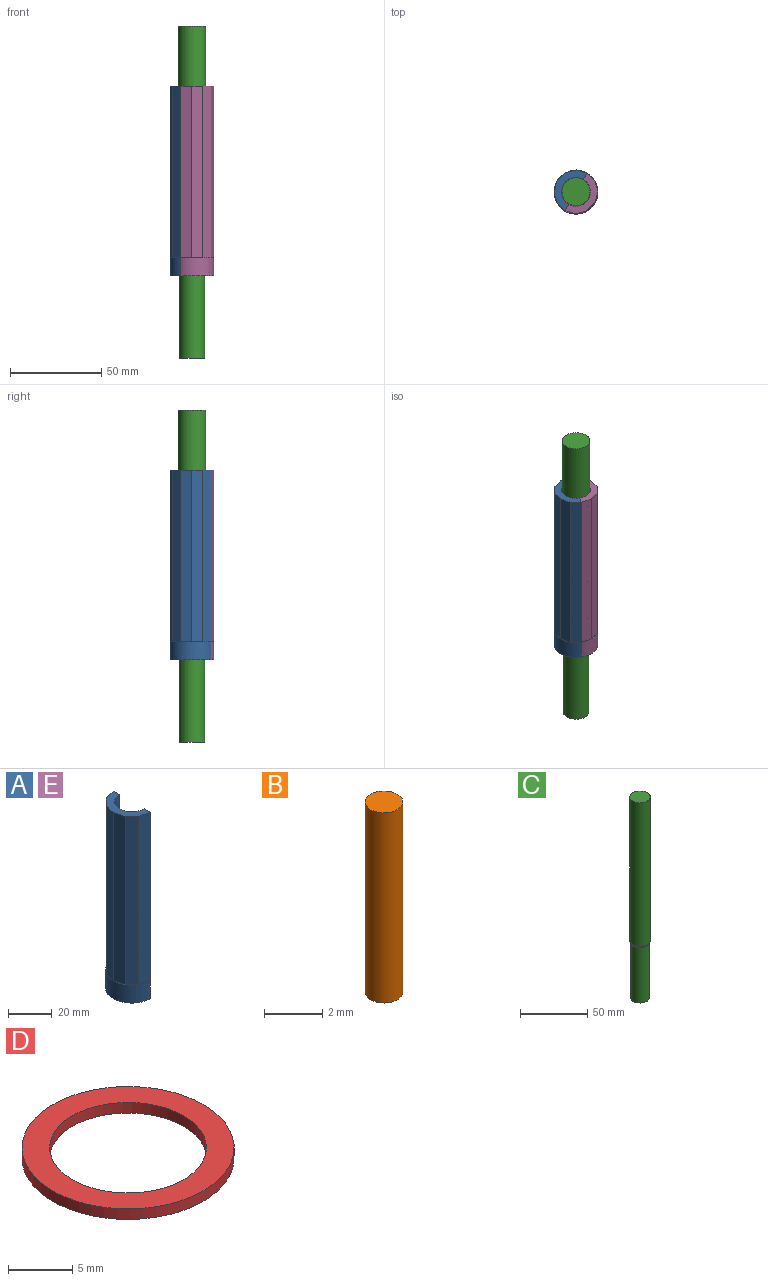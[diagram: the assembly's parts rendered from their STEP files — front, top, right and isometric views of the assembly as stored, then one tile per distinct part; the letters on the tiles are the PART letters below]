
ASSEMBLY  parts=5 mates=4
PART A: 38 faces, bbox 12x24x104 mm
  f0: plane 104x4.1mm, normal (1,0,0), area 417.7mm2, adj f11,f13,f14,f15,f16,f17,f18,f19
  f1: plane 94x4.39mm, normal (-0.71,-0.71,0), area 583.9mm2, adj f2,f9,f11,f12
  f2: plane 94x6mm, normal (-0.97,-0.26,0), area 583.9mm2, adj f1,f3,f8,f11
  f3: plane 94x6mm, normal (-0.97,0.26,0), area 583.9mm2, adj f2,f4,f7,f11
  f4: plane 94x4.39mm, normal (-0.71,0.71,0), area 583.9mm2, adj f3,f6,f11,f13
  f5: plane 6x1.61mm, normal (0,0,1), area 1.7mm2, adj f13,f19
  f6: plane 4.39x4.39mm, normal (0,0,1), area 1.7mm2, adj f4,f19
  f7: plane 6x1.61mm, normal (0,0,1), area 1.7mm2, adj f3,f19
  f8: plane 6x1.61mm, normal (0,0,1), area 1.7mm2, adj f2,f19
  f9: plane 4.39x4.39mm, normal (0,0,1), area 1.7mm2, adj f1,f19
  f10: plane 6x1.61mm, normal (0,0,1), area 1.7mm2, adj f12,f19
  f11: plane 24x12mm, normal (0,0,1), area 118mm2, adj f0,f1,f2,f3,f4,f12,f13,f20
  f12: plane 94x6mm, normal (-0.26,-0.97,0), area 583.9mm2, adj f1,f10,f11,f21
  f13: plane 94x6mm, normal (-0.26,0.97,0), area 583.9mm2, adj f0,f4,f5,f11
  f14: cylinder r=8.75mm len=17.5mm, axis (0,0,1), area 110mm2, adj f0,f15,f16,f21
  f15: plane 17.5x8.75mm, normal (0,0,-1), area 22.2mm2, adj f0,f14,f20,f21
  f16: plane 17.5x8.75mm, normal (0,0,1), area 22.2mm2, adj f0,f14,f17,f21
  f17: cylinder r=7.9mm len=15.8mm, axis (0,0,-1), area 74.5mm2, adj f0,f16,f18,f21
  f18: plane 24x12mm, normal (0,0,-1), area 128.2mm2, adj f0,f17,f19,f21
  f19: cylinder r=12mm len=24mm, axis (0,0,1), area 377mm2, adj f0,f5,f6,f7,f8,f9,f10,f18
  f20: cylinder r=7.9mm len=97mm, axis (0,0,-1), area 2407.4mm2, adj f0,f11,f15,f21
  f21: plane 104x4.1mm, normal (1,0,0), area 417.7mm2, adj f11,f12,f14,f15,f16,f17,f18,f19
  f22: cylinder r=0.65mm len=4mm, axis (1,0,0), area 16.3mm2, adj f21,f23
  f23: plane 1.3x1.3mm, normal (1,0,0), area 1.3mm2, adj f22
  f24: cylinder r=0.65mm len=4mm, axis (1,0,0), area 16.3mm2, adj f21,f25
  f25: plane 1.3x1.3mm, normal (1,0,0), area 1.3mm2, adj f24
  f26: cylinder r=0.65mm len=4mm, axis (1,0,0), area 16.3mm2, adj f21,f27
  f27: plane 1.3x1.3mm, normal (1,0,0), area 1.3mm2, adj f26
  f28: cylinder r=0.65mm len=4mm, axis (1,0,0), area 16.3mm2, adj f21,f29
  f29: plane 1.3x1.3mm, normal (1,0,0), area 1.3mm2, adj f28
  f30: cylinder r=0.65mm len=4mm, axis (1,0,0), area 16.3mm2, adj f0,f31
  f31: plane 1.3x1.3mm, normal (1,0,0), area 1.3mm2, adj f30
  f32: cylinder r=0.65mm len=4mm, axis (1,0,0), area 16.3mm2, adj f0,f33
  f33: plane 1.3x1.3mm, normal (1,0,0), area 1.3mm2, adj f32
  f34: cylinder r=0.65mm len=4mm, axis (1,0,0), area 16.3mm2, adj f0,f35
  f35: plane 1.3x1.3mm, normal (1,0,0), area 1.3mm2, adj f34
  f36: cylinder r=0.65mm len=4mm, axis (1,0,0), area 16.3mm2, adj f0,f37
  f37: plane 1.3x1.3mm, normal (1,0,0), area 1.3mm2, adj f36
PART B: 3 faces, bbox 1.3x1.3x8 mm
  f0: cylinder r=0.65mm len=8mm, axis (0,0,-1), area 32.7mm2, adj f1,f2
  f1: plane 1.3x1.3mm, normal (0,0,1), area 1.3mm2, adj f0
  f2: plane 1.3x1.3mm, normal (0,0,-1), area 1.3mm2, adj f0
PART C: 7 faces, bbox 15.3x15.3x182 mm
  f0: cylinder r=7mm len=50mm, axis (0,0,-1), area 2199.1mm2, adj f1,f2
  f1: plane 14x14mm, normal (0,0,1), area 40.8mm2, adj f0,f3
  f2: plane 14x14mm, normal (0,0,-1), area 153.9mm2, adj f0
  f3: cylinder r=6mm len=12mm, axis (0,0,-1), area 75.4mm2, adj f1,f6
  f4: cylinder r=7.65mm len=130mm, axis (0,0,-1), area 6248.6mm2, adj f5,f6
  f5: plane 15.3x15.3mm, normal (0,0,1), area 183.9mm2, adj f4
  f6: plane 15.3x15.3mm, normal (0,0,-1), area 70.8mm2, adj f3,f4
PART D: 4 faces, bbox 16.5x16.5x1 mm
  f0: cylinder r=6.1mm len=12.2mm, axis (0,0,-1), area 38.3mm2, adj f2,f3
  f1: cylinder r=8.25mm len=16.5mm, axis (0,0,-1), area 51.8mm2, adj f2,f3
  f2: plane 16.5x16.5mm, normal (0,0,1), area 96.9mm2, adj f0,f1
  f3: plane 16.5x16.5mm, normal (0,0,-1), area 96.9mm2, adj f0,f1
PART E: same geometry as A
PLACE A rot(axis=(0,0,-1),30.6deg) t=(1.16,1.81,90.67)mm
PLACE B rot(axis=(-0.78,-0.44,0.44),104.2deg) t=(-0.49,-8.84,105.23)mm
PLACE C rot(axis=(0,0,-1),30.6deg) t=(1.16,1.81,35.67)mm fixed
PLACE D rot(axis=(0,0,-1),30.6deg) t=(1.16,1.81,86.67)mm
PLACE E rot(axis=(0,0,1),149.4deg) t=(1.16,1.81,90.67)mm
MATE slider C.f4 <-> A.f17  axis (0,0,-1) through (1.16,1.81,87.67)mm
MATE fastened E.f30 <-> B.f0  axis (-0.86,0.51,0) through (-0.49,-8.84,105.23)mm
MATE fastened A.f28 <-> B.f0  axis (0.86,-0.51,0) through (-7.38,-4.77,105.23)mm
MATE cylindrical D.f1 <-> C.f3  axis (0,0,1) through (1.16,1.81,87.67)mm
